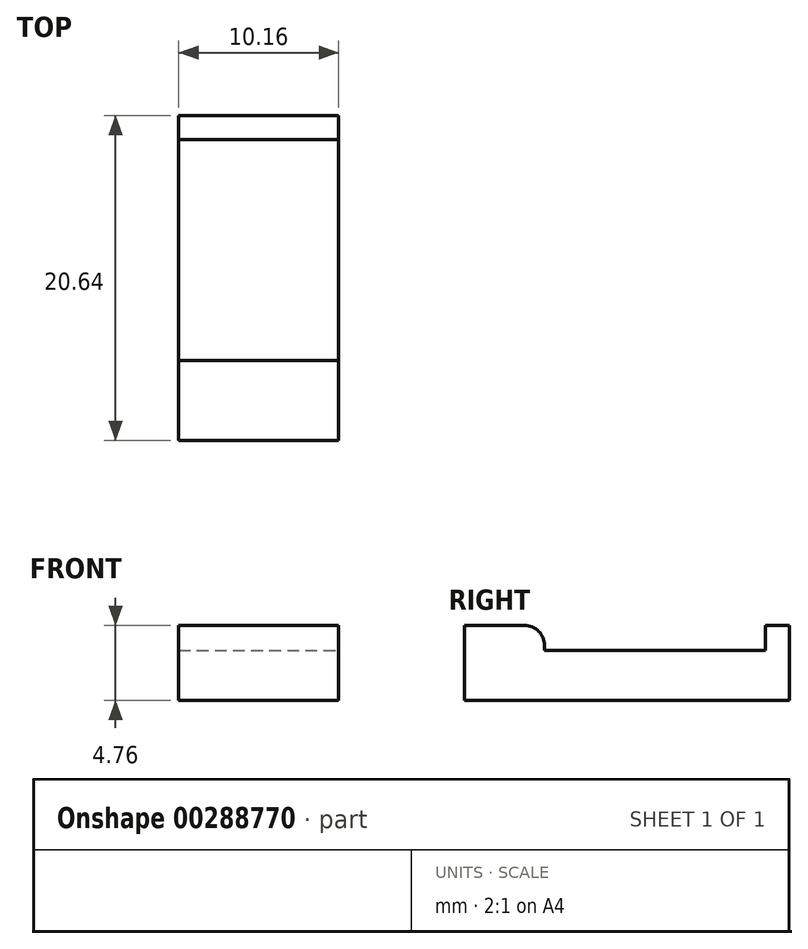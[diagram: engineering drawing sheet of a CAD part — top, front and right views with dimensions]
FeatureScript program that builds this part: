
annotation { "Feature Type Name" : "Feature", "Feature Type Description" : "" }
export const myFeature = defineFeature(function(context is Context, id is Id, definition is map)
    precondition{}
    {
        {
            var Q0;
            Q0=qCreatedBy(makeId("Top.planeOp"),FACE);
            var sketch = newSketch(context, id + "F0", { "sketchPlane" : qUnion([Q0])});
            skLineSegment(sketch, "E0.bottom", {"start": v(-5.08, 10.32) * mm, "end": v(5.08, 10.32) * mm});
            skLineSegment(sketch, "E0.top", {"start": v(-5.08, -10.32) * mm, "end": v(5.08, -10.32) * mm});
            skLineSegment(sketch, "E0.left", {"start": v(-5.08, 10.32) * mm, "end": v(-5.08, -10.32) * mm});
            skLineSegment(sketch, "E0.right", {"start": v(5.08, 10.32) * mm, "end": v(5.08, -10.32) * mm});
            skPoint(sketch, "E0.middle", {"position": v(0, 0) * mm});
            skLineSegment(sketch, "E1", {"start": v(-5.08, -5.24) * mm, "end": v(5.08, -5.24) * mm});
            skLineSegment(sketch, "E2", {"start": v(-5.08, 8.8) * mm, "end": v(5.08, 8.8) * mm});
            skSolve(sketch);
        }
        {
            var Q0;
            {var subQ0=sQuery(id+"F0.wireOp",EDGE,"E1");Q0=makeQuery(id+"F0.imprint","IMPRINT",FACE,{"disambiguationData":[TD([[makeQuery(id+"F0.imprint","IMPRINT",EDGE,{"derivedFrom":subQ0}),1.0]])]});}
            extrude(context, id + "F1", {"entities" : qUnion([Q0]), "depth" : 3.17 * mm});
        }
        {
            var Q0;
            {var subQ0=sQuery(id+"F0.wireOp",EDGE,"E0.top");Q0=makeQuery(id+"F0.imprint","IMPRINT",FACE,{"disambiguationData":[TD([[makeQuery(id+"F0.imprint","IMPRINT",EDGE,{"derivedFrom":subQ0}),1.0]])]});}
            var Q1;
            {var subQ0=sQuery(id+"F0.wireOp",EDGE,"E0.bottom");Q1=makeQuery(id+"F0.imprint","IMPRINT",FACE,{"disambiguationData":[TD([[makeQuery(id+"F0.imprint","IMPRINT",EDGE,{"derivedFrom":subQ0}),-1.0]])]});}
            extrude(context, id + "F2", {"entities" : qUnion([Q0, Q1]), "operationType" : NewBodyOperationType.ADD, "depth" : 4.76 * mm});
        }
        {
            var Q0;
            Q0=makeQuery(id+"F2.opExtrude","CAP_EDGE",EDGE,{"disambiguationData":[OSD([sQuery(id+"F0.wireOp",EDGE,"E1")])],"isStart":false});
            fillet(context, id + "F3", {"entities" : qUnion([Q0]), "radius" : 1.27 * mm, "tangentPropagation" : true, "allowEdgeOverflow" : false});
        }
    });
